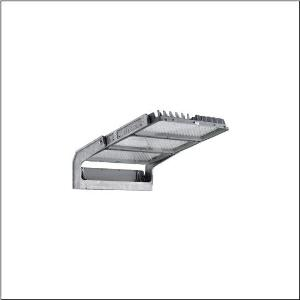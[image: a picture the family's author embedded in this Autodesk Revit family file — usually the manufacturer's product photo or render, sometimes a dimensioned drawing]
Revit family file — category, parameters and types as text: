
# Revit family: floodlight_fl_11_maxi_pro___rs07_5xa779129k01gb_3319
name_source: partatom
category: Lighting Fixtures
units: mm (PartAtom-declared; Revit-internal decimal feet)

## family parameters
Cut with Voids When Loaded = No
Host = Face
Light Source = No
Part Type = Normal
Room Calculation Point = No
Round Connector Dimension = Use Diameter
Shared = No

## types (1)
- --- (1 x LED, 164870 lm, 1315 W, 5700K)
    Apparent Load = 1315 VA
    CIE Flux Codes = 80 93 99 100 99
    Color Rendering = 70
    Color Temperature = 5700K
    Default Elevation = 1800 mm
    Description = Floodlight FL 11  maxi  pro floodlight; light control with lens of PMMA; cover panel of toughened safety glass, transparent; light distribution: RS07, rotationally symmetric direct distribution, LED; colour temperature: 5700K, rated luminous flux: 164.870lm, colour rendering: CRI > 70, light colour: 757; luminous efficacy: 125lm/W; brightness control: DALI 2; with terminal, 5-pole, max. 2.5mm², mains connection: 220..240V/380..400V AC, 50/60Hz, surge voltage resistance: line to ground: 10kV, LED service life up to 100,000h L90. Typical operating time: 1000h per year., ECG replaceable separately, LED unit replaceable without ESD environment, dustproof LED module, dimming range 10..100%; 1315W floodlight with 3x LED unit of diecast aluminium, coated grey; length: 1.003mm / width: 651mm / height: 338mm; mounting bracket, of diecast aluminium, uncoated, natural, equipment: Power, protection rating (complete): IP66; insulation class (complete): insulation class I (protective earthing); certification: CE, ENEC, VDE; ball protection: ball impact resistant, only for outdoor installations in the designated locations, permissible operating ambient temperature: -45..+55°C, permissible storage temperature: -40..+85°Cpackaging unit: 1 piece

Light Distribution: RS07
    Height = 320 mm
    Lamp = 1 x LED
    Lamp Light Flux = 164870 lm
    Lamp Power = 1315 W
    Lamp count = 1
    Length = 1002 mm
    Luminous efficacy = 125 lm/W
    Manufacturer = Siteco
    ModVariant = No
    Model = 5XA779129K01GB
    Mounting Place = Ceiling
    Mounting Type = Surface mounted
    Number of Poles = 1
    OnlyDefault = Yes
    Power Factor = 1
    Product Name = Floodlight FL 11 maxi pro | RS07
    Product group = floodlight | ceiling mounted
    ProductGroupID = 303
    Protection Class = Protection class I
    Protection Degree = IP 66
    RLX_Detail_Level = 1
    RLX_Emergency_Light_Flux = 0 lm
    RLX_Emergency_Type = 0
    RLX_Emergency_Type_DB = No
    RlxData = <blob elided: 40321 chars, md5=32578054>
    Socket = socket
    Standby Power = 0 W
    System Light Flux = 164870 lm
    System Power = 1315 W
    Type Comments = factory setting: luminous flux: 100 % | dim-lin: 254 | 895 mA
    Type Image = l_1356210.jpg
    URL = http://relux.com
    VarID = @adj_038969
    Voltage = 0 V
    Weight = 0.00 kg
    Width = 655 mm

## geometry (parser evidence)
native form markers: Blend x4, Sweep x11
no freeform markers — native parametric forms only
